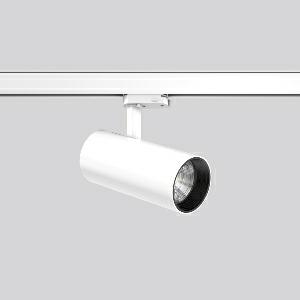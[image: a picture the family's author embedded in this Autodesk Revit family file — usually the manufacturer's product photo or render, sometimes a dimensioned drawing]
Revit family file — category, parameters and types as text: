
# Revit family: deecos_s_mini_742198_002_76_d030
name_source: partatom
category: Lighting Fixtures
units: mm (PartAtom-declared; Revit-internal decimal feet)

## family parameters
Cut with Voids When Loaded = No
Host = Face
Light Source = No
Part Type = Normal
Room Calculation Point = No
Round Connector Dimension = Use Diameter
Shared = No

## types (1)
- DEECOS S mini (1 x LED Modul 930, 2250 lm, 3000)
    Apparent Load = 20 VA
    Approval mark = CE
    CIE Flux Codes = 99 100 100 100 100
    Color Rendering = 90
    Color Temperature = 3000
    Default Elevation = 1800 mm
    Description = Series: DEECOS S mini
LED surface-mounted projector in modern design with no visible cooling ribs. Housing: die-cast aluminium, powder-coated. Rotation range: 356°. Swivel range: 90°. Black plastic ring and recessed LED to prevent glare from the side. Optical assembly with lens made of plastic (polycarbonate) for the best homogeneous light distribution - can be changed without tools. Best colour rendering index Ra>90. With adapter for RZB 3-circuit DALI tracks. Suitable for Track on ceiling, Wall track. High quality converter without flickering and stroboscopic effect. The following accessories can be mounted without use of tools: interchangeable lenses, decorative glasses, honeycomb louvre, clear and frosted diffusers, white interchangeable plastic ring. 
Colour: traffic white, matt (RAL 9016)
Diameter: 87 mm
Height: 214 mm
Lamp: LED
Socket: without socket
Colour temperature: 3000K
Colour rendering index (CRI): 92
System power: 20 W
Rated luminous flux: 2250 lm
Luminous efficiency: 113 lm/W
Control gear: Converter, dimmable, DALI
Protection class: I
Type of protection: IP 20
    Height = 214 mm
    Lamp = 1 x LED Modul 930
    Lamp Light Flux = 2250 lm
    Lamp count = 1
    Length = 87 mm
    Lifetime = 50000 h
    Luminous efficacy = 113 lm/W
    Manufacturer = RZB
    ModVariant = No
    Model = 742198.002.76
    Mounting Place = Ceiling
    Mounting Type = Rail mounted
    Number of Poles = 1
    OnlyDefault = Yes
    Power Factor = 1
    Product Name = DEECOS S mini
    Product group = Track mounted projectors
    ProductGroupID = 301
    Protection Class = Protection class I
    Protection Degree = IP 20
    RLX_Detail_Level = 1
    RLX_Emergency_Light_Flux = 0 lm
    RLX_Emergency_Type = 0
    RLX_Emergency_Type_DB = No
    RlxData = <blob elided: 35381 chars, md5=7cdd10d2>
    Socket = socket
    Standby Power = 0 W
    System Light Flux = 2250 lm
    System Power = 20 W
    Type Comments = Product without accessories
    Type Image = 741930.002.jpg
    URL = http://relux.com
    VarID = ---
    Voltage = 230 V
    Voltage Range = 220-240 V
    Weight = 0.00 kg
    Width = 0 mm  [stored 0 ft]

note: [stored X ft] marks values corroborated as IEEE doubles in the binary element streams (Revit-internal decimal feet)

## geometry (parser evidence)
native form markers: Blend x4, Sweep x12
no freeform markers — native parametric forms only
